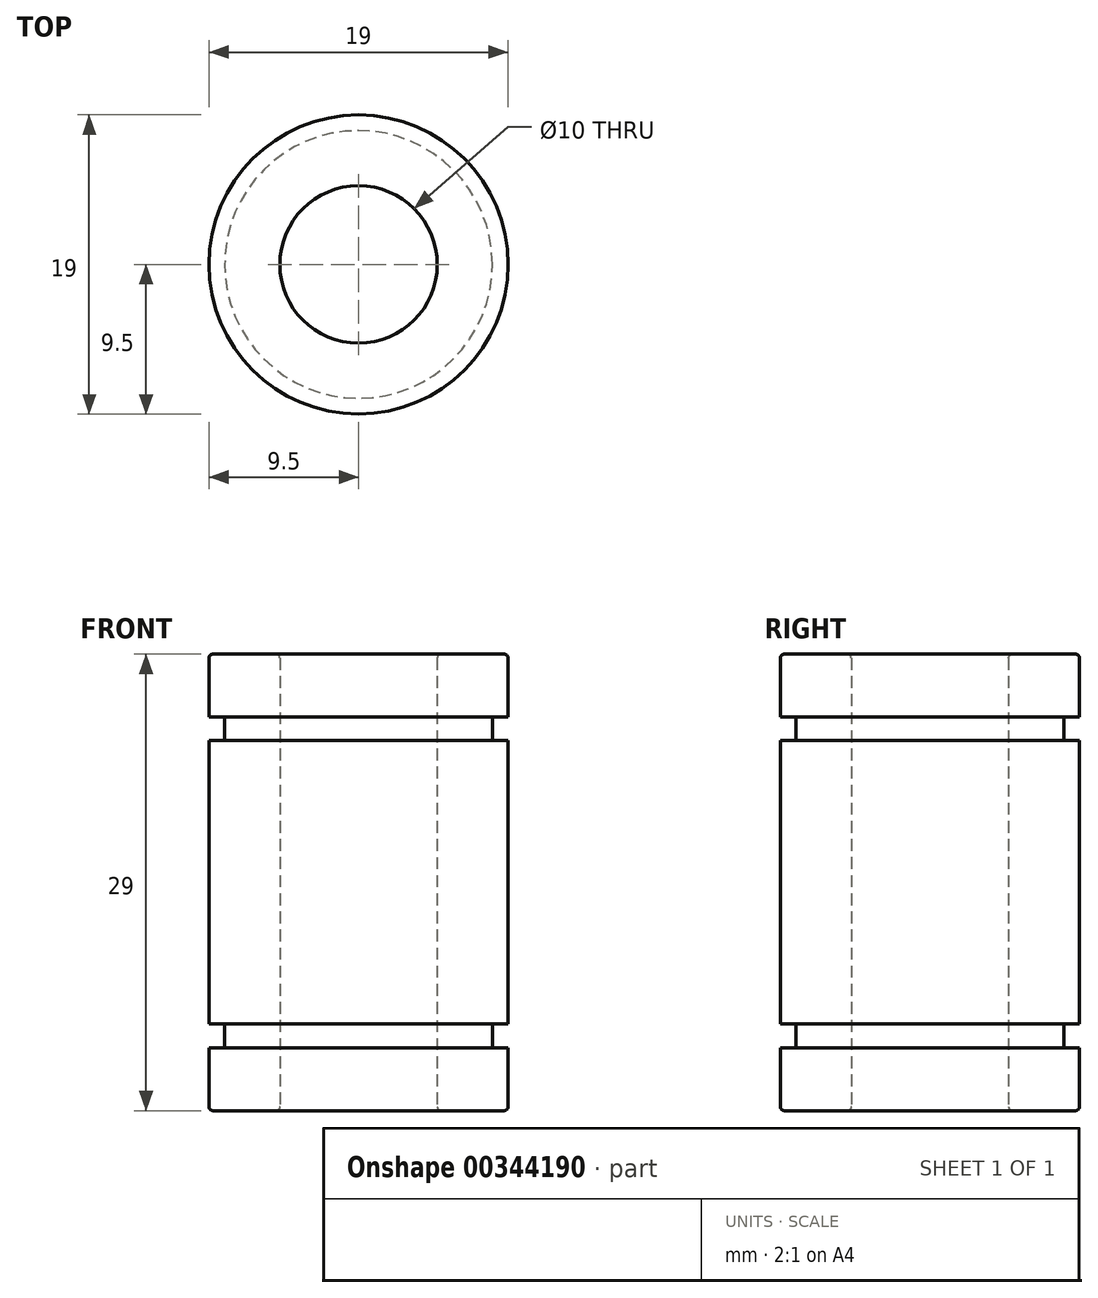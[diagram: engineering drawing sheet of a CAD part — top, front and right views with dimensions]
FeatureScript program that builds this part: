
annotation { "Feature Type Name" : "Feature", "Feature Type Description" : "" }
export const myFeature = defineFeature(function(context is Context, id is Id, definition is map)
    precondition{}
    {
        {
            var Q0;
            Q0=qCreatedBy(makeId("Top.planeOp"),FACE);
            var sketch = newSketch(context, id + "F0", { "sketchPlane" : qUnion([Q0])});
            skCircle(sketch, "E0", {"center": v(0, 0) * mm, "radius": 5 * mm});
            skCircle(sketch, "E1", {"center": v(0, 0) * mm, "radius": 9.5 * mm});
            skSolve(sketch);
        }
        {
            var Q0;
            Q0 = qSketchRegion(id + "F0", true);
            extrude(context, id + "F1", {"entities" : qUnion([Q0]), "depth" : 29 * mm});
        }
        {
            var Q0;
            Q0=makeQuery(id+"F1.opExtrude","CAP_FACE",FACE,{"disambiguationData":[OSD([sQuery(id+"F0.wireOp",EDGE,"E0"),sQuery(id+"F0.wireOp",EDGE,"E1")])],"isStart":false});
            var Q1;
            Q1=makeQuery(id+"F1.opExtrude","CAP_FACE",FACE,{"disambiguationData":[OSD([sQuery(id+"F0.wireOp",EDGE,"E0"),sQuery(id+"F0.wireOp",EDGE,"E1")])],"isStart":true});
            fillet(context, id + "F2", {"entities" : qUnion([Q0, Q1]), "radius" : .25 * mm, "tangentPropagation" : true, "allowEdgeOverflow" : false});
        }
        {
            var Q0;
            Q0=qCreatedBy(makeId("Front.planeOp"),FACE);
            var sketch = newSketch(context, id + "F3", { "sketchPlane" : qUnion([Q0])});
            skLineSegment(sketch, "E2", {"start": v(0, -1.05) * mm, "end": v(0, 48.03) * mm, "construction": true});
            skLineSegment(sketch, "E3.bottom", {"start": v(8.5, 25) * mm, "end": v(11.5, 25) * mm});
            skLineSegment(sketch, "E3.top", {"start": v(8.5, 23.5) * mm, "end": v(11.5, 23.5) * mm});
            skLineSegment(sketch, "E3.left", {"start": v(8.5, 25) * mm, "end": v(8.5, 23.5) * mm});
            skLineSegment(sketch, "E3.right", {"start": v(11.5, 25) * mm, "end": v(11.5, 23.5) * mm});
            skLineSegment(sketch, "E4.bottom", {"start": v(8.5, 5.5) * mm, "end": v(11.5, 5.5) * mm});
            skLineSegment(sketch, "E4.top", {"start": v(8.5, 4) * mm, "end": v(11.5, 4) * mm});
            skLineSegment(sketch, "E4.left", {"start": v(8.5, 5.5) * mm, "end": v(8.5, 4) * mm});
            skLineSegment(sketch, "E4.right", {"start": v(11.5, 5.5) * mm, "end": v(11.5, 4) * mm});
            skSolve(sketch);
        }
        {
            var Q0;
            Q0 = qSketchRegion(id + "F3", true);
            var Q1;
            Q1=sQuery(id+"F3.wireOp",EDGE,"E2");
            revolve(context, id + "F4", {"operationType" : NewBodyOperationType.REMOVE, "entities" : qUnion([Q0]), "axis" : qUnion([Q1]), "revolveType" : RevolveType.FULL, "oppositeDirection" : true});
        }
    });
